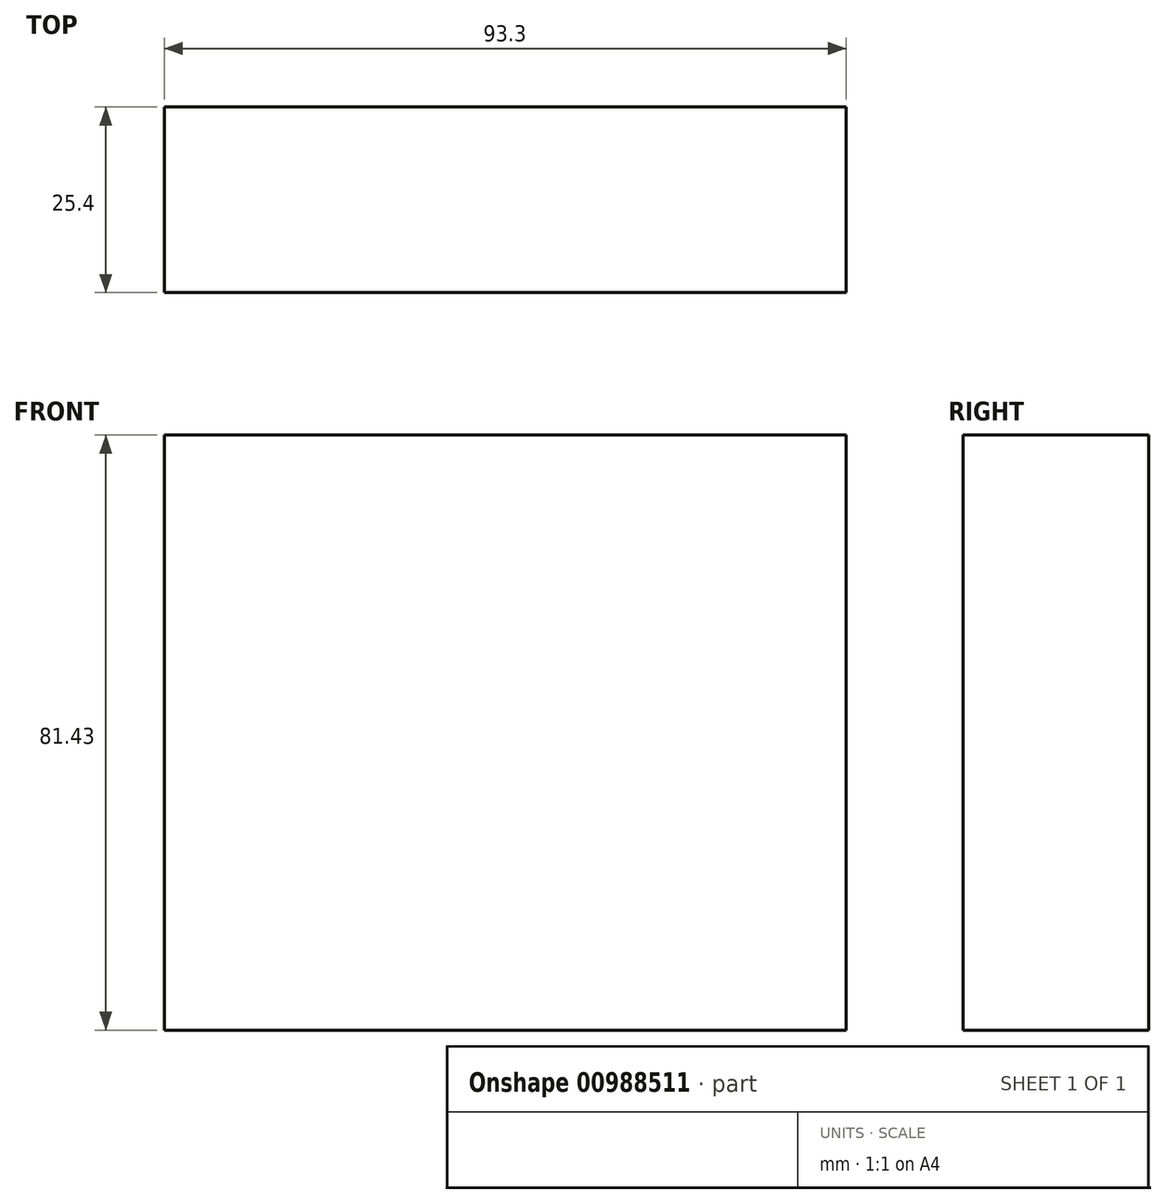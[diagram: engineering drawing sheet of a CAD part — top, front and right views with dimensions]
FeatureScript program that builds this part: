
annotation { "Feature Type Name" : "Feature", "Feature Type Description" : "" }
export const myFeature = defineFeature(function(context is Context, id is Id, definition is map)
    precondition{}
    {
        {
            var Q0;
            Q0=qCreatedBy(makeId("Front.planeOp"),FACE);
            var sketch = newSketch(context, id + "F0", { "sketchPlane" : qUnion([Q0])});
            skLineSegment(sketch, "E0.bottom", {"start": v(48.57, 59.84) * mm, "end": v(-44.73, 59.84) * mm});
            skLineSegment(sketch, "E0.top", {"start": v(48.57, -21.6) * mm, "end": v(-44.73, -21.6) * mm});
            skLineSegment(sketch, "E0.left", {"start": v(48.57, 59.84) * mm, "end": v(48.57, -21.6) * mm});
            skLineSegment(sketch, "E0.right", {"start": v(-44.73, 59.84) * mm, "end": v(-44.73, -21.6) * mm});
            skSolve(sketch);
        }
        {
            var Q0;
            Q0=makeQuery(id+"F0.imprint","IMPRINT",FACE,{"disambiguationData":[TD([[makeQuery(id+"F0.imprint","IMPRINT",EDGE,{"derivedFrom":sQuery(id+"F0.wireOp",EDGE,"E0.bottom")}),1.0]])]});
            extrude(context, id + "F1", {"entities" : qUnion([Q0]), "depth" : 25.4 * mm, "offsetDistance" : 25.4 * mm});
        }
    });
